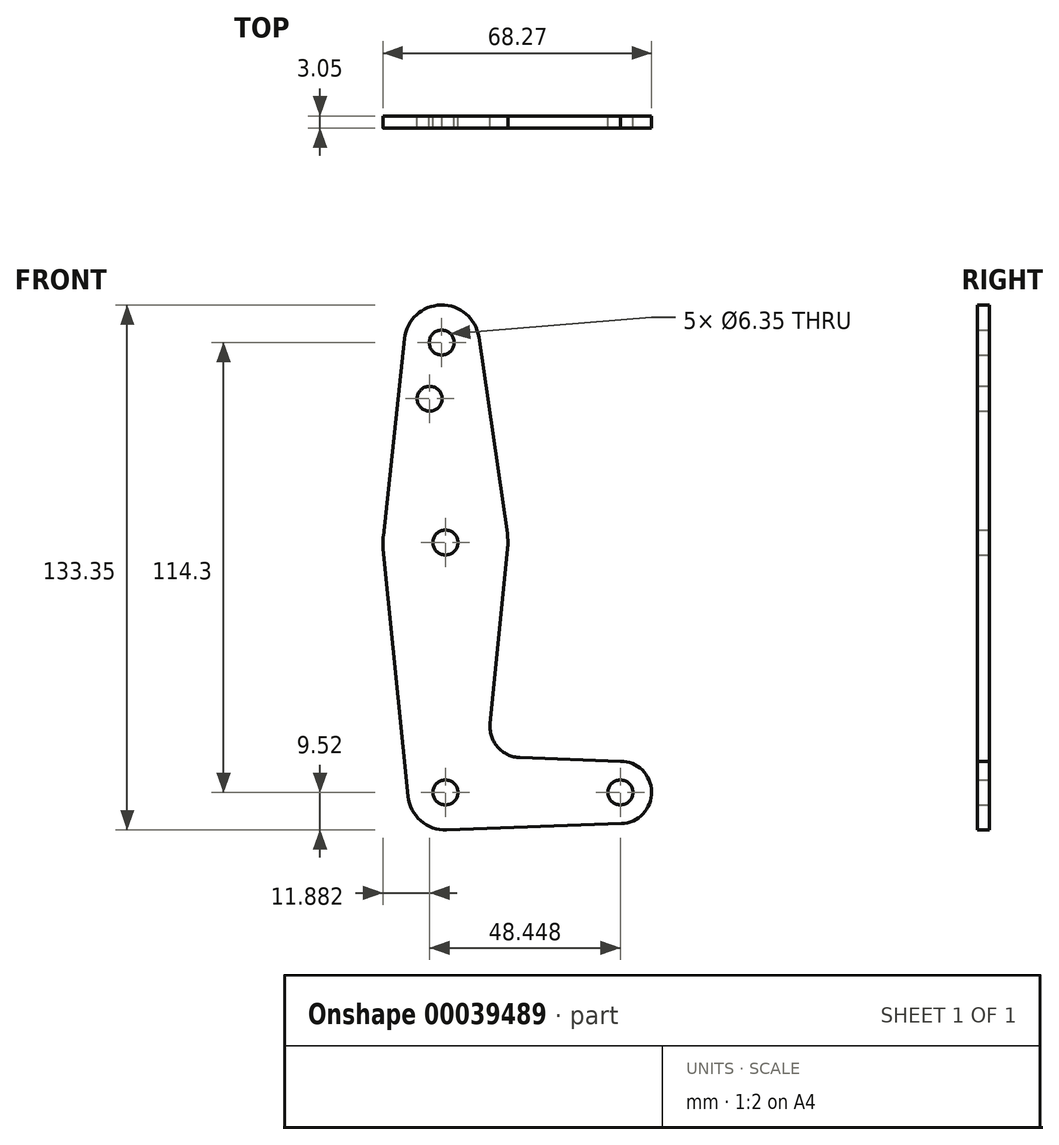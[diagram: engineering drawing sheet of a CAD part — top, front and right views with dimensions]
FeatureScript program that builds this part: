
annotation { "Feature Type Name" : "Feature", "Feature Type Description" : "" }
export const myFeature = defineFeature(function(context is Context, id is Id, definition is map)
    precondition{}
    {
        {
            var Q0;
            Q0=qCreatedBy(makeId("Front.planeOp"),FACE);
            var sketch = newSketch(context, id + "F0", { "sketchPlane" : qUnion([Q0])});
            skCircle(sketch, "E0", {"center": v(0, 63.5) * mm, "radius": 15.88 * mm});
            skCircle(sketch, "E1", {"center": v(-0.94, 114.3) * mm, "radius": 9.53 * mm});
            skCircle(sketch, "E2", {"center": v(0, 0) * mm, "radius": 9.53 * mm});
            skCircle(sketch, "E3", {"center": v(44.45, 0) * mm, "radius": 7.94 * mm});
            skLineSegment(sketch, "E4", {"start": v(0, 0) * mm, "end": v(44.45, 0) * mm, "construction": true});
            skLineSegment(sketch, "E5", {"start": v(0, 0) * mm, "end": v(-0.94, 114.3) * mm, "construction": true});
            skLineSegment(sketch, "E6", {"start": v(-10.41, 115.32) * mm, "end": v(-15.78, 65.2) * mm});
            skLineSegment(sketch, "E7", {"start": v(-15.8, 61.91) * mm, "end": v(-9.48, -0.95) * mm});
            skLineSegment(sketch, "E8", {"start": v(11.34, 17.6) * mm, "end": v(15.8, 61.91) * mm});
            skLineSegment(sketch, "E9", {"start": v(8.49, 115.67) * mm, "end": v(15.71, 65.78) * mm});
            skLineSegment(sketch, "E10", {"start": v(44.45, 7.94) * mm, "end": v(18.97, 8.85) * mm});
            skLineSegment(sketch, "E11", {"start": v(0.34, -9.52) * mm, "end": v(44.73, -7.93) * mm});
            skCircle(sketch, "E12", {"center": v(-0.94, 114.3) * mm, "radius": 3.18 * mm});
            skCircle(sketch, "E13", {"center": v(-4, 100.03) * mm, "radius": 3.18 * mm});
            skCircle(sketch, "E14", {"center": v(0, 63.5) * mm, "radius": 3.18 * mm});
            skCircle(sketch, "E15", {"center": v(0, 0) * mm, "radius": 3.18 * mm});
            skCircle(sketch, "E16", {"center": v(44.45, 0) * mm, "radius": 3.18 * mm});
            skArc(sketch, "E17.filletArc", {"start": v(11.34, 17.6) * mm, "mid": v(13.26, 11.57) * mm, "end": v(18.97, 8.85) * mm});
            skSolve(sketch);
        }
        {
            var Q0;
            Q0 = qSketchRegion(id + "F0", true);
            extrude(context, id + "F1", {"entities" : qUnion([Q0]), "depth" : 3.05 * mm});
        }
    });
